# Revit family: IS_Tipica_T2380_BIM_NL
name_source: partatom
category: Plumbing Fixtures
revit_build: Autodesk Revit MEP 2014 (Build: 20130308_1515(x64)
units: mm (PartAtom-declared; Revit-internal decimal feet)

## types (1)
- T2380YB - TIPICA HOEKINSTAP CABINE 90X90CM
    Accessories = www.idealstandardnederland.nl
    AreaUnits = millimeters
    Assembly Code = C1030200
    AssetType = Vast
    BIMObjectName = ISI_IdealStandard_ShowerEnclosures_T2380YB
    BREEAM = No
    Brand = Ideal Standard
    Color = Zilverkleurig
    Cost = 0 $
    Default Elevation = 0 mm  [stored 0 ft]
    Description = Tipica hoekinstap cabine. Hoogte 1850 mm. 3 mm transparant veiligheidsglas. Met aluminium muurprofiel. Verchroomde greep. Horizontale aanpassing tot 25 mm.

Installatie: dit is een complete hoekinstap.
    DrainSize = 38 mm
    DurationUnit = jaar
    ECA = No
    ExpectedLife = 25
    Features = Hoekinstap cabine. Hoogte 1850 mm. 3 mm transparant veiligheidsglas. Met aluminium muurprofiel. Verchroomde greep. Horizontale aanpassing tot 25 mm.

Installatie: dit is een complete hoekinstap.
    Finish = Zilverkleurig
    HWFU = 0
    HasRiserKit = No
    HasTray = Yes
    IfcExportAs = IfcSanitaryTerminalType
    IfcExportType = SHOWER
    InstallationInstructions = http://www.idealstandardnederland.nl
    LinearUnits = millimeters
    ManufacturerURL = www.idealstandardnederland.nl
    Material = Glas
    MaterialThickness = 0 mm  [stored 0 ft]
    Model = T2380YB
    ModelNumber = T2380YB
    ModelReference = Tipica hoekinstap cabine. Hoogte 1850 mm. 3 mm transparant veiligheidsglas. Met aluminium muurprofiel. Verchroomde greep. Horizontale aanpassing tot 25 mm.

Installatie: dit is een complete hoekinstap.
    NBSDescription = Shower enclosures
    NBSReference = 45-35-70/332
    Name = ShowerEnclosures_T2380YB_IdealStandard
    NettWeight = 34.1 kg
    NominalDepth = 900 mm  [stored 2.95276 ft]
    NominalHeight = 1850 mm
    NominalLength = 900 mm  [stored 2.95276 ft]
    NominalWidth = 900 mm  [stored 2.95276 ft]
    ProductInformation = http://www.idealstandardnederland.nl
    Shape = Gesculptuurd
    ShowerType = Individual
    Size = 900 x 1850 x 900 mm
    Space = Internal
    SpareParts = www.idealstandardnederland.nl
    TMV3 = No
    TrayMatl = ISI_IdealStandard_ShowerTray_White_Render
    URL = www.idealstandardnederland.nl
    Uniclass2015Code = Pr_40_20_06_79
    Uniclass2015Title = Shower enclosures
    Uniclass2015Version = Products v1.1
    Version = 1
    VolumeUnits = liter
    WRAS = No
    WarrantyDescription = Fabrieksgarantie
    WarrantyDurationParts = 5
    WarrantyDurationUnit = jaar
    WasteMatl = ISI_IdealStandard_Shower_Chrome_Render
    WaterEfficientProduct = No

note: [stored X ft] marks values corroborated as IEEE doubles in the binary element streams (Revit-internal decimal feet)

## geometry (parser evidence)
native form markers: Blend x2, Sweep x3
no freeform markers — native parametric forms only
